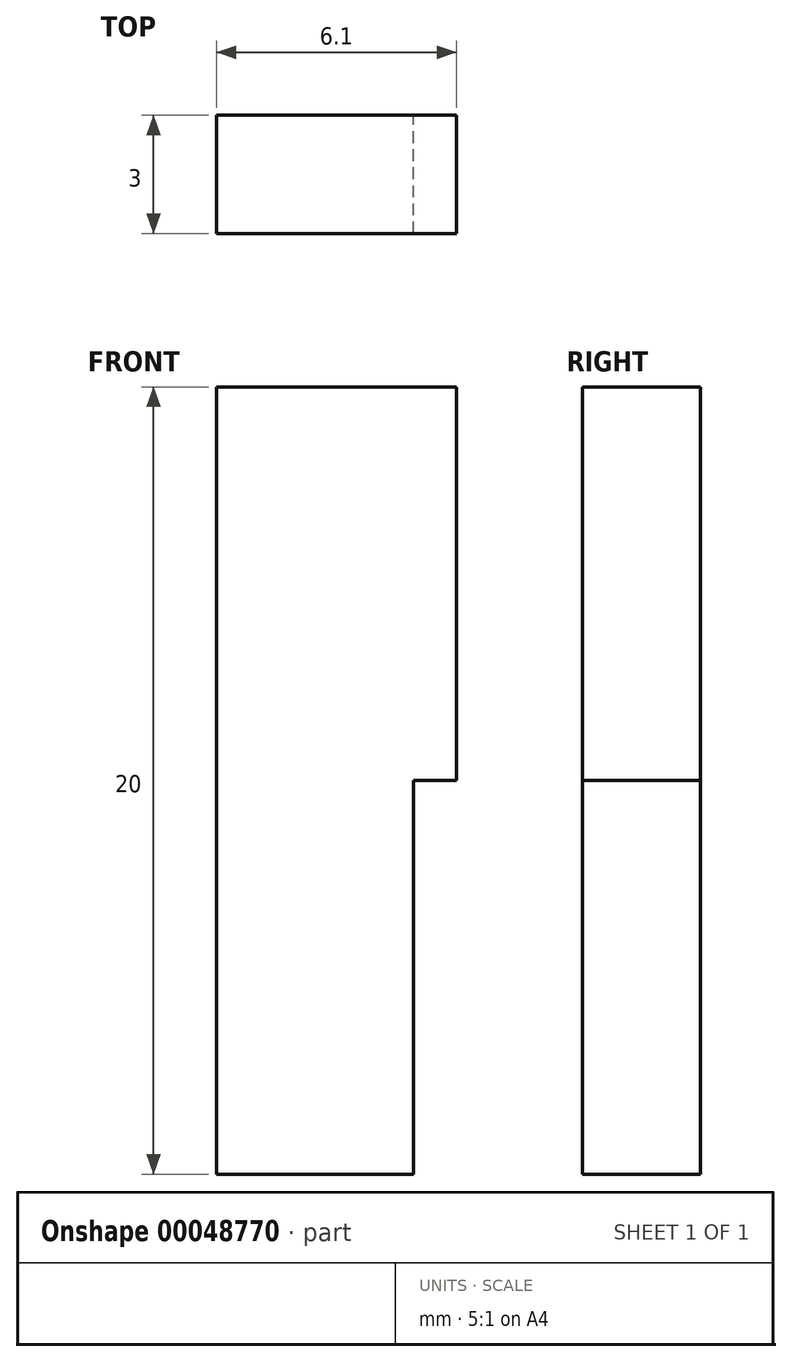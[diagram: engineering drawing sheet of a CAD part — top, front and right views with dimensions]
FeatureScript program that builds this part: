
annotation { "Feature Type Name" : "Feature", "Feature Type Description" : "" }
export const myFeature = defineFeature(function(context is Context, id is Id, definition is map)
    precondition{}
    {
        {
            var Q0;
            Q0=qCreatedBy(makeId("Front.planeOp"),FACE);
            var sketch = newSketch(context, id + "F0", { "sketchPlane" : qUnion([Q0])});
            skLineSegment(sketch, "E0", {"start": v(0, 0) * mm, "end": v(0, 20) * mm});
            skLineSegment(sketch, "E1", {"start": v(0, 20) * mm, "end": v(6.1, 20) * mm});
            skLineSegment(sketch, "E2", {"start": v(6.1, 20) * mm, "end": v(6.1, 10) * mm});
            skLineSegment(sketch, "E3", {"start": v(6.1, 10) * mm, "end": v(5, 10) * mm});
            skLineSegment(sketch, "E4", {"start": v(5, 10) * mm, "end": v(5, 0) * mm});
            skLineSegment(sketch, "E5", {"start": v(5, 0) * mm, "end": v(0, 0) * mm});
            skSolve(sketch);
        }
        {
            var Q0;
            Q0=makeQuery(id+"F0.imprint","IMPRINT",FACE,{"disambiguationData":[TD([[makeQuery(id+"F0.imprint","IMPRINT",EDGE,{"derivedFrom":sQuery(id+"F0.wireOp",EDGE,"E0")}),-1.0]])]});
            extrude(context, id + "F1", {"entities" : qUnion([Q0]), "depth" : 3 * mm});
        }
    });
